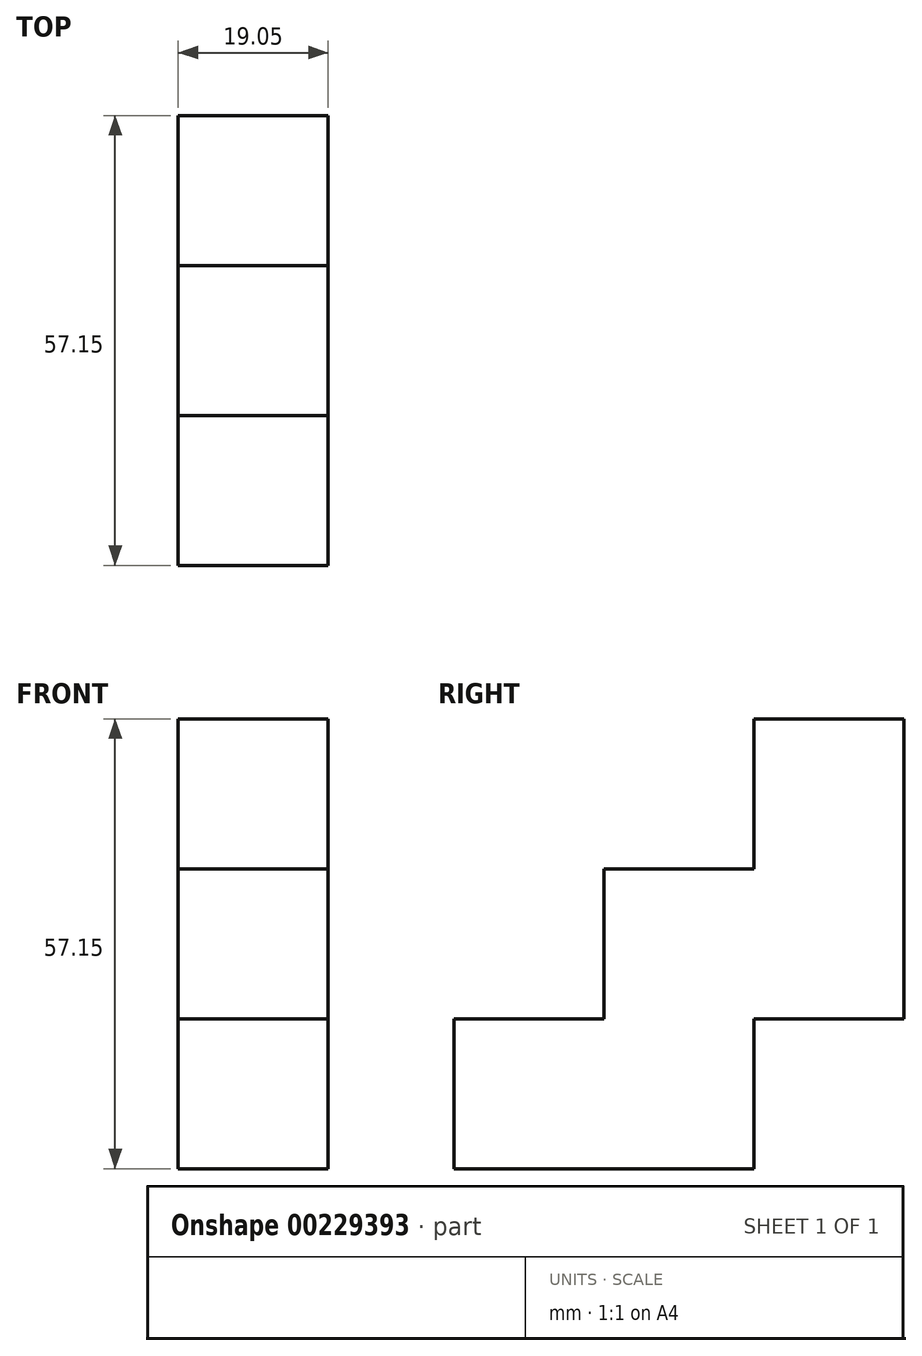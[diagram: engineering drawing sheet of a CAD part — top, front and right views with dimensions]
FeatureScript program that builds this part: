
annotation { "Feature Type Name" : "Feature", "Feature Type Description" : "" }
export const myFeature = defineFeature(function(context is Context, id is Id, definition is map)
    precondition{}
    {
        {
            var Q0;
            Q0=qCreatedBy(makeId("Front.planeOp"),FACE);
            var sketch = newSketch(context, id + "F0", { "sketchPlane" : qUnion([Q0])});
            skLineSegment(sketch, "E0.bottom", {"start": v(-12.27, 33.29) * mm, "end": v(6.78, 33.29) * mm});
            skLineSegment(sketch, "E0.top", {"start": v(-12.27, -4.81) * mm, "end": v(6.78, -4.81) * mm});
            skLineSegment(sketch, "E0.left", {"start": v(-12.27, 33.29) * mm, "end": v(-12.27, -4.81) * mm});
            skLineSegment(sketch, "E0.right", {"start": v(6.78, 33.29) * mm, "end": v(6.78, -4.81) * mm});
            skSolve(sketch);
        }
        {
            var Q0;
            Q0=makeQuery(id+"F0.imprint","IMPRINT",FACE,{"disambiguationData":[TD([[makeQuery(id+"F0.imprint","IMPRINT",EDGE,{"derivedFrom":sQuery(id+"F0.wireOp",EDGE,"E0.bottom")}),-1.0]])]});
            extrude(context, id + "F1", {"entities" : qUnion([Q0]), "depth" : 19.05 * mm});
        }
        {
            var Q0;
            Q0=makeQuery(id+"F1.opExtrude","CAP_FACE",FACE,{"disambiguationData":[OSD([sQuery(id+"F0.wireOp",EDGE,"E0.bottom"),sQuery(id+"F0.wireOp",EDGE,"E0.top"),sQuery(id+"F0.wireOp",EDGE,"E0.left"),sQuery(id+"F0.wireOp",EDGE,"E0.right")])],"isStart":false});
            var sketch = newSketch(context, id + "F2", { "sketchPlane" : qUnion([Q0])});
            skLineSegment(sketch, "E1.bottom", {"start": v(-12.27, -4.81) * mm, "end": v(6.78, -4.81) * mm});
            skLineSegment(sketch, "E1.top", {"start": v(-12.27, 14.24) * mm, "end": v(6.78, 14.24) * mm});
            skLineSegment(sketch, "E1.left", {"start": v(-12.27, -4.81) * mm, "end": v(-12.27, 14.24) * mm});
            skLineSegment(sketch, "E1.right", {"start": v(6.78, -4.81) * mm, "end": v(6.78, 14.24) * mm});
            skSolve(sketch);
        }
        {
            var Q0;
            Q0=makeQuery(id+"F2.imprint","IMPRINT",FACE,{"disambiguationData":[TD([[makeQuery(id+"F2.imprint","IMPRINT",EDGE,{"derivedFrom":sQuery(id+"F2.wireOp",EDGE,"E1.bottom")}),1.0]])]});
            extrude(context, id + "F3", {"entities" : qUnion([Q0]), "operationType" : NewBodyOperationType.ADD, "depth" : 19.05 * mm});
        }
        {
            var Q0;
            Q0=makeQuery(id+"F3.boolean.opBoolean","MERGE",FACE,{"derivedFrom":[makeQuery(id+"F1.opExtrude","SWEPT_FACE",FACE,{"disambiguationData":[OSD([sQuery(id+"F0.wireOp",EDGE,"E0.top")])]}),makeQuery(id+"F3.opExtrude","SWEPT_FACE",FACE,{"disambiguationData":[OSD([sQuery(id+"F2.wireOp",EDGE,"E1.bottom")])]})]});
            var sketch = newSketch(context, id + "F4", { "sketchPlane" : qUnion([Q0])});
            skLineSegment(sketch, "E2.bottom", {"start": v(-12.27, 38.1) * mm, "end": v(6.78, 38.1) * mm});
            skLineSegment(sketch, "E2.top", {"start": v(-12.27, 19.05) * mm, "end": v(6.78, 19.05) * mm});
            skLineSegment(sketch, "E2.left", {"start": v(-12.27, 38.1) * mm, "end": v(-12.27, 19.05) * mm});
            skLineSegment(sketch, "E2.right", {"start": v(6.78, 38.1) * mm, "end": v(6.78, 19.05) * mm});
            skSolve(sketch);
        }
        {
            var Q0;
            Q0=makeQuery(id+"F4.imprint","IMPRINT",FACE,{"disambiguationData":[TD([[makeQuery(id+"F4.imprint","IMPRINT",EDGE,{"derivedFrom":sQuery(id+"F4.wireOp",EDGE,"E2.bottom")}),-1.0]])]});
            extrude(context, id + "F5", {"entities" : qUnion([Q0]), "operationType" : NewBodyOperationType.ADD, "depth" : 19.05 * mm});
        }
        {
            var Q0;
            Q0=makeQuery(id+"F5.boolean.opBoolean","MERGE",FACE,{"derivedFrom":[makeQuery(id+"F3.opExtrude","CAP_FACE",FACE,{"disambiguationData":[OSD([sQuery(id+"F2.wireOp",EDGE,"E1.bottom"),sQuery(id+"F2.wireOp",EDGE,"E1.top"),sQuery(id+"F2.wireOp",EDGE,"E1.left"),sQuery(id+"F2.wireOp",EDGE,"E1.right")])],"isStart":false}),makeQuery(id+"F5.opExtrude","SWEPT_FACE",FACE,{"disambiguationData":[OSD([sQuery(id+"F4.wireOp",EDGE,"E2.bottom")])]})]});
            var sketch = newSketch(context, id + "F6", { "sketchPlane" : qUnion([Q0])});
            skLineSegment(sketch, "E3.bottom", {"start": v(-12.27, -4.81) * mm, "end": v(6.78, -4.81) * mm});
            skLineSegment(sketch, "E3.top", {"start": v(-12.27, -23.86) * mm, "end": v(6.78, -23.86) * mm});
            skLineSegment(sketch, "E3.left", {"start": v(-12.27, -4.81) * mm, "end": v(-12.27, -23.86) * mm});
            skLineSegment(sketch, "E3.right", {"start": v(6.78, -4.81) * mm, "end": v(6.78, -23.86) * mm});
            skSolve(sketch);
        }
        {
            var Q0;
            Q0 = qSketchRegion(id + "F6", true);
            var Q1;
            Q1=makeQuery(id+"F6.imprint","IMPRINT",FACE,{"disambiguationData":[TD([[makeQuery(id+"F6.imprint","IMPRINT",EDGE,{"derivedFrom":sQuery(id+"F6.wireOp",EDGE,"E3.bottom")}),-1.0]])]});
            extrude(context, id + "F7", {"entities" : qUnion([Q0, Q1]), "operationType" : NewBodyOperationType.ADD, "depth" : 19.05 * mm});
        }
    });
